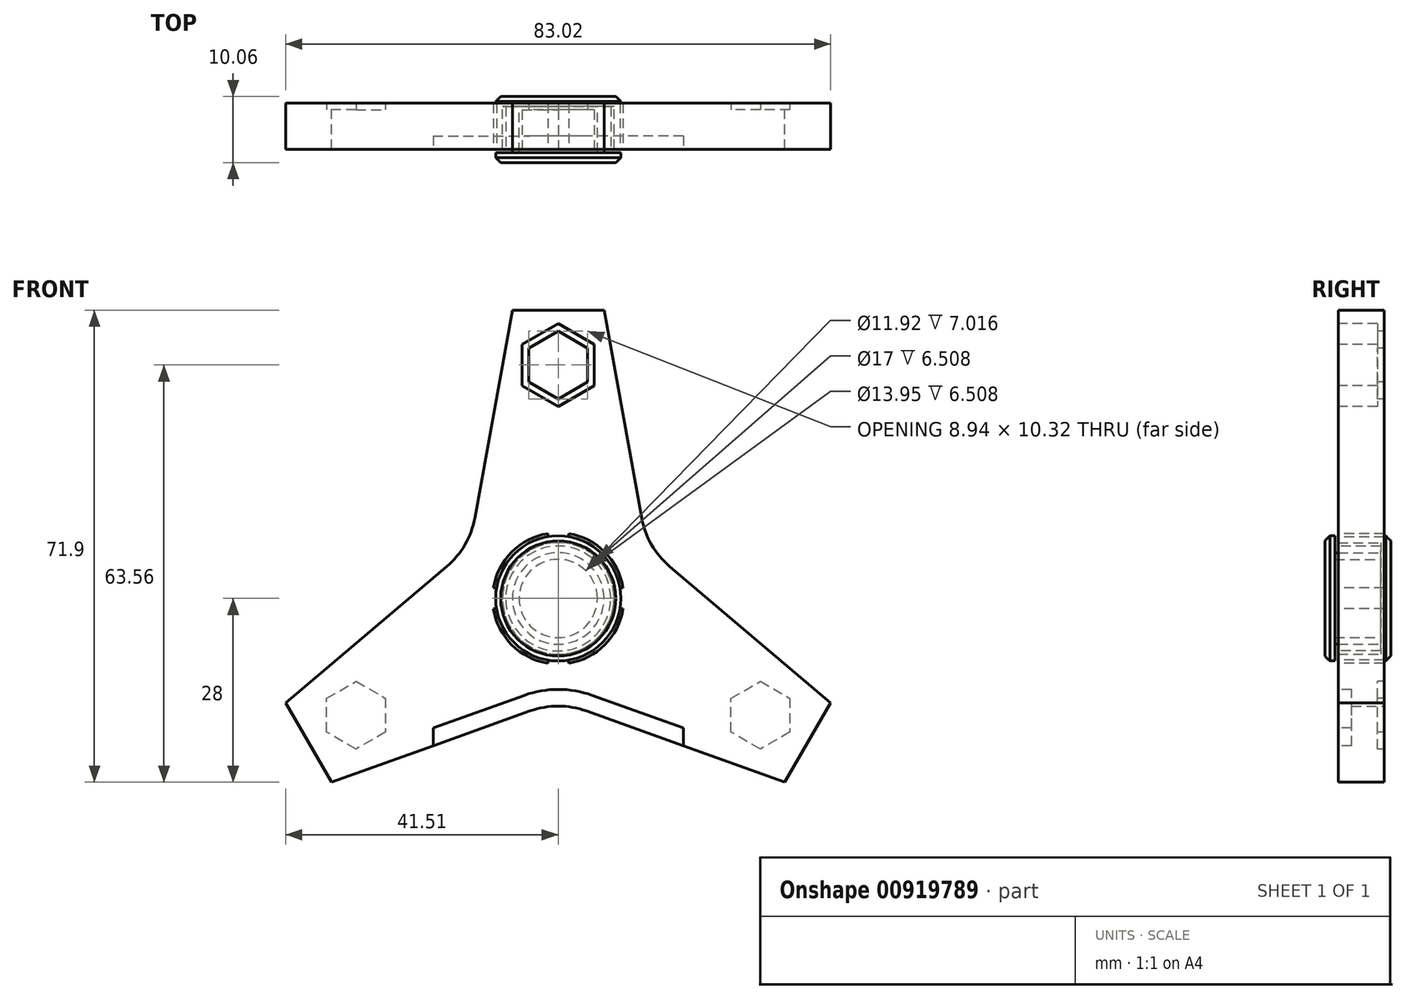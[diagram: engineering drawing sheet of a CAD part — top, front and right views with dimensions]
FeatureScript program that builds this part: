
annotation { "Feature Type Name" : "Feature", "Feature Type Description" : "" }
export const myFeature = defineFeature(function(context is Context, id is Id, definition is map)
    precondition{}
    {
        {
            var Q0;
            Q0=qCreatedBy(makeId("Front.planeOp"),FACE);
            var sketch = newSketch(context, id + "F0", { "sketchPlane" : qUnion([Q0])});
            skCircle(sketch, "E0", {"center": v(0, 0) * mm, "radius": 8.5 * mm});
            skCircle(sketch, "E1.cCircle", {"center": v(0, 0) * mm, "radius": 44.45 * mm, "construction": true});
            skPoint(sketch, "E1.0.midPoint", {"position": v(-38.62, -22) * mm});
            skLineSegment(sketch, "E2", {"start": v(-6.99, 43.9) * mm, "end": v(6.99, 43.9) * mm});
            skLineSegment(sketch, "E3", {"start": v(6.98, 43.9) * mm, "end": v(12.7, 12.29) * mm});
            skLineSegment(sketch, "E4", {"start": v(-6.98, 43.9) * mm, "end": v(-12.7, 12.29) * mm});
            skLineSegment(sketch, "E5.1.0", {"start": v(41.5, -15.9) * mm, "end": v(17, 4.85) * mm});
            skLineSegment(sketch, "E5.1.1", {"start": v(34.52, -28) * mm, "end": v(4.3, -17.14) * mm});
            skLineSegment(sketch, "E5.1.2", {"start": v(41.5, -15.9) * mm, "end": v(34.52, -28) * mm});
            skLineSegment(sketch, "E5.2.0", {"start": v(-34.52, -28) * mm, "end": v(-4.3, -17.14) * mm});
            skLineSegment(sketch, "E5.2.1", {"start": v(-41.5, -15.9) * mm, "end": v(-17, 4.85) * mm});
            skLineSegment(sketch, "E5.2.2", {"start": v(-34.52, -28) * mm, "end": v(-41.5, -15.9) * mm});
            skLineSegment(sketch, "E5.anchor1", {"start": v(0, 0) * mm, "end": v(-14.92, 0) * mm, "construction": true});
            skLineSegment(sketch, "E5.anchor2", {"start": v(0, 0) * mm, "end": v(7.46, -12.92) * mm, "construction": true});
            skPoint(sketch, "E6.orphan", {"position": v(-7.46, 12.92) * mm});
            skPoint(sketch, "E7.orphan", {"position": v(7.46, 12.92) * mm});
            skPoint(sketch, "E8.orphan", {"position": v(-7.46, -12.92) * mm});
            skPoint(sketch, "E9.orphan", {"position": v(14.92, 0) * mm});
            skPoint(sketch, "E10.visualSharp", {"position": v(-13.51, 7.8) * mm});
            skArc(sketch, "E10.filletArc", {"start": v(-17, 4.85) * mm, "mid": v(-14.2, 8.2) * mm, "end": v(-12.7, 12.29) * mm});
            skPoint(sketch, "E11.visualSharp", {"position": v(13.51, 7.8) * mm});
            skArc(sketch, "E11.filletArc", {"start": v(12.7, 12.29) * mm, "mid": v(14.2, 8.2) * mm, "end": v(17, 4.85) * mm});
            skPoint(sketch, "E12.visualSharp", {"position": v(0, -15.6) * mm});
            skArc(sketch, "E12.filletArc", {"start": v(4.3, -17.14) * mm, "mid": v(0, -16.4) * mm, "end": v(-4.3, -17.14) * mm});
            skSolve(sketch);
        }
        {
            var Q0;
            Q0=makeQuery(id+"F0.imprint","IMPRINT",FACE,{"disambiguationData":[TD([[makeQuery(id+"F0.imprint","IMPRINT",EDGE,{"derivedFrom":sQuery(id+"F0.wireOp",EDGE,"E0")}),-1.0]])]});
            extrude(context, id + "F1", {"entities" : qUnion([Q0]), "depth" : 6 * mm, "offsetDistance" : 25.4 * mm});
        }
        {
            var Q0;
            Q0=makeQuery(id+"F1.opExtrude","CAP_FACE",FACE,{"disambiguationData":[OSD([sQuery(id+"F0.wireOp",EDGE,"E0"),sQuery(id+"F0.wireOp",EDGE,"E2"),sQuery(id+"F0.wireOp",EDGE,"E3"),sQuery(id+"F0.wireOp",EDGE,"E4"),sQuery(id+"F0.wireOp",EDGE,"E5.1.0"),sQuery(id+"F0.wireOp",EDGE,"E5.1.1"),sQuery(id+"F0.wireOp",EDGE,"E5.1.2"),sQuery(id+"F0.wireOp",EDGE,"E5.2.0"),sQuery(id+"F0.wireOp",EDGE,"E5.2.1"),sQuery(id+"F0.wireOp",EDGE,"E5.2.2"),sQuery(id+"F0.wireOp",EDGE,"E10.filletArc"),sQuery(id+"F0.wireOp",EDGE,"E11.filletArc"),sQuery(id+"F0.wireOp",EDGE,"E12.filletArc")])],"isStart":false});
            var sketch = newSketch(context, id + "F2", { "sketchPlane" : qUnion([Q0])});
            skCircle(sketch, "E13.0", {"center": v(0, 0) * mm, "radius": 8 * mm});
            skCircle(sketch, "E14.0", {"center": v(0, 0) * mm, "radius": 6.98 * mm});
            skSolve(sketch);
        }
        {
            var Q0;
            Q0=makeQuery(id+"F2.imprint","IMPRINT",FACE,{"disambiguationData":[TD([[makeQuery(id+"F2.imprint","IMPRINT",EDGE,{"derivedFrom":sQuery(id+"F2.wireOp",EDGE,"E13.0")}),1.0]])]});
            var Q1;
            Q1=makeQuery(id+"F1.opExtrude","CAP_FACE",FACE,{"disambiguationData":[OSD([sQuery(id+"F0.wireOp",EDGE,"E0"),sQuery(id+"F0.wireOp",EDGE,"E2"),sQuery(id+"F0.wireOp",EDGE,"E3"),sQuery(id+"F0.wireOp",EDGE,"E4"),sQuery(id+"F0.wireOp",EDGE,"E5.1.0"),sQuery(id+"F0.wireOp",EDGE,"E5.1.1"),sQuery(id+"F0.wireOp",EDGE,"E5.1.2"),sQuery(id+"F0.wireOp",EDGE,"E5.2.0"),sQuery(id+"F0.wireOp",EDGE,"E5.2.1"),sQuery(id+"F0.wireOp",EDGE,"E5.2.2"),sQuery(id+"F0.wireOp",EDGE,"E10.filletArc"),sQuery(id+"F0.wireOp",EDGE,"E11.filletArc"),sQuery(id+"F0.wireOp",EDGE,"E12.filletArc")])],"isStart":true});
            extrude(context, id + "F3", {"entities" : qUnion([Q0]), "endBound" : BoundingType.UP_TO_SURFACE, "oppositeDirection" : true, "depth" : 25.4 * mm, "endBoundEntityFace" : qUnion([Q1]), "hasOffset" : true, "offsetDistance" : 0.5 * mm, "offsetOppositeDirection" : true});
        }
        {
            var Q0;
            Q0=makeQuery(id+"F3.opExtrude","CAP_FACE",FACE,{"disambiguationData":[OSD([sQuery(id+"F2.wireOp",EDGE,"E13.0"),sQuery(id+"F2.wireOp",EDGE,"E14.0")])],"isStart":false});
            var sketch = newSketch(context, id + "F4", { "sketchPlane" : qUnion([Q0])});
            skCircle(sketch, "E15", {"center": v(0, 0) * mm, "radius": 9.53 * mm});
            skSolve(sketch);
        }
        {
            var Q0;
            Q0=makeQuery(id+"F4.imprint","IMPRINT",FACE,{"disambiguationData":[TD([[makeQuery(id+"F4.imprint","IMPRINT",EDGE,{"derivedFrom":sQuery(id+"F4.wireOp",EDGE,"E15")}),1.0]])]});
            var Q1;
            Q1=makeQuery(id+"F4.imprint","IMPRINT",FACE,{"disambiguationData":[TD([[makeQuery(id+"F4.imprint","IMPRINT",EDGE,{"derivedFrom":makeQuery(id+"F3.opExtrude","CAP_EDGE",EDGE,{"disambiguationData":[OSD([sQuery(id+"F2.wireOp",EDGE,"E14.0")])],"isStart":false})}),1.0]])]});
            var Q2;
            Q2=makeQuery(id+"F4.imprint","IMPRINT",FACE,{"disambiguationData":[TD([[makeQuery(id+"F4.imprint","IMPRINT",EDGE,{"derivedFrom":makeQuery(id+"F3.opExtrude","CAP_EDGE",EDGE,{"disambiguationData":[OSD([sQuery(id+"F2.wireOp",EDGE,"E13.0")])],"isStart":false})}),1.0]])]});
            var Q3;
            Q3=sQuery(id+"F4.wireOp",EDGE,"E15");
            extrude(context, id + "F5", {"entities" : qUnion([Q0, Q1, Q2]), "operationType" : NewBodyOperationType.ADD, "surfaceOperationType" : NewSurfaceOperationType.ADD, "surfaceEntities" : qUnion([Q3]), "depth" : 1.52 * mm, "offsetDistance" : 25.4 * mm});
        }
        {
            var Q0;
            Q0=makeQuery(id+"F5.boolean.opBoolean","SPLIT",FACE,{"disambiguationData":[TD([makeQuery(id+"F3.opExtrude","SWEPT_FACE",FACE,{"disambiguationData":[OSD([sQuery(id+"F2.wireOp",EDGE,"E14.0")])]})])],"derivedFrom":makeQuery(id+"F5.opExtrude","CAP_FACE",FACE,{"disambiguationData":[OSD([sQuery(id+"F4.wireOp",EDGE,"E15")])],"isStart":true})});
            var sketch = newSketch(context, id + "F6", { "sketchPlane" : qUnion([Q0])});
            skCircle(sketch, "E16.0", {"center": v(0, 0) * mm, "radius": 6.98 * mm});
            skCircle(sketch, "E17.0", {"center": v(0, 0) * mm, "radius": 5.96 * mm});
            skSolve(sketch);
        }
        {
            var Q0;
            Q0=makeQuery(id+"F6.imprint","IMPRINT",FACE,{"disambiguationData":[TD([[makeQuery(id+"F6.imprint","IMPRINT",EDGE,{"derivedFrom":sQuery(id+"F6.wireOp",EDGE,"E16.0")}),-1.0]])]});
            var Q1;
            Q1=sQuery(id+"F6.wireOp",EDGE,"E16.0");
            var Q2;
            Q2=makeQuery(id+"F1.opExtrude","CAP_FACE",FACE,{"disambiguationData":[OSD([sQuery(id+"F0.wireOp",EDGE,"E0"),sQuery(id+"F0.wireOp",EDGE,"E2"),sQuery(id+"F0.wireOp",EDGE,"E3"),sQuery(id+"F0.wireOp",EDGE,"E4"),sQuery(id+"F0.wireOp",EDGE,"E5.1.0"),sQuery(id+"F0.wireOp",EDGE,"E5.1.1"),sQuery(id+"F0.wireOp",EDGE,"E5.1.2"),sQuery(id+"F0.wireOp",EDGE,"E5.2.0"),sQuery(id+"F0.wireOp",EDGE,"E5.2.1"),sQuery(id+"F0.wireOp",EDGE,"E5.2.2"),sQuery(id+"F0.wireOp",EDGE,"E10.filletArc"),sQuery(id+"F0.wireOp",EDGE,"E11.filletArc"),sQuery(id+"F0.wireOp",EDGE,"E12.filletArc")])],"isStart":false});
            extrude(context, id + "F7", {"entities" : qUnion([Q0]), "surfaceEntities" : qUnion([Q1]), "endBound" : BoundingType.UP_TO_SURFACE, "depth" : 25.4 * mm, "endBoundEntityFace" : qUnion([Q2]), "hasOffset" : true, "offsetDistance" : 0.5 * mm, "offsetOppositeDirection" : true});
        }
        {
            var Q0;
            Q0=makeQuery(id+"F7.opExtrude","CAP_FACE",FACE,{"disambiguationData":[OSD([sQuery(id+"F6.wireOp",EDGE,"E16.0"),sQuery(id+"F6.wireOp",EDGE,"E17.0")])],"isStart":false});
            var sketch = newSketch(context, id + "F8", { "sketchPlane" : qUnion([Q0])});
            skCircle(sketch, "E18.0", {"center": v(0, 0) * mm, "radius": 9.53 * mm});
            skSolve(sketch);
        }
        {
            var Q0;
            Q0=makeQuery(id+"F8.imprint","IMPRINT",FACE,{"disambiguationData":[TD([[makeQuery(id+"F8.imprint","IMPRINT",EDGE,{"derivedFrom":sQuery(id+"F8.wireOp",EDGE,"E18.0")}),1.0]])]});
            var Q1;
            Q1=makeQuery(id+"F8.imprint","IMPRINT",FACE,{"disambiguationData":[TD([[makeQuery(id+"F8.imprint","IMPRINT",EDGE,{"derivedFrom":makeQuery(id+"F7.opExtrude","CAP_EDGE",EDGE,{"disambiguationData":[OSD([sQuery(id+"F6.wireOp",EDGE,"E16.0")])],"isStart":false})}),-1.0]])]});
            var Q2;
            Q2=makeQuery(id+"F8.imprint","IMPRINT",FACE,{"disambiguationData":[TD([[makeQuery(id+"F8.imprint","IMPRINT",EDGE,{"derivedFrom":makeQuery(id+"F7.opExtrude","CAP_EDGE",EDGE,{"disambiguationData":[OSD([sQuery(id+"F6.wireOp",EDGE,"E17.0")])],"isStart":false})}),1.0]])]});
            extrude(context, id + "F9", {"entities" : qUnion([Q0, Q1, Q2]), "operationType" : NewBodyOperationType.ADD, "depth" : 1.52 * mm, "offsetDistance" : 25.4 * mm});
        }
        {
            var Q0;
            Q0=makeQuery(id+"F5.opExtrude","CAP_EDGE",EDGE,{"disambiguationData":[OSD([sQuery(id+"F4.wireOp",EDGE,"E15")])],"isStart":false});
            var Q1;
            Q1=makeQuery(id+"F9.opExtrude","CAP_EDGE",EDGE,{"disambiguationData":[OSD([sQuery(id+"F8.wireOp",EDGE,"E18.0")])],"isStart":false});
            chamfer(context, id + "F10", {"entities" : qUnion([Q0, Q1]), "width" : 0.76 * mm, "tangentPropagation" : true});
        }
        {
            var Q0;
            Q0=makeQuery(id+"F1.opExtrude","CAP_FACE",FACE,{"disambiguationData":[OSD([sQuery(id+"F0.wireOp",EDGE,"E0"),sQuery(id+"F0.wireOp",EDGE,"E2"),sQuery(id+"F0.wireOp",EDGE,"E3"),sQuery(id+"F0.wireOp",EDGE,"E4"),sQuery(id+"F0.wireOp",EDGE,"E5.1.0"),sQuery(id+"F0.wireOp",EDGE,"E5.1.1"),sQuery(id+"F0.wireOp",EDGE,"E5.1.2"),sQuery(id+"F0.wireOp",EDGE,"E5.2.0"),sQuery(id+"F0.wireOp",EDGE,"E5.2.1"),sQuery(id+"F0.wireOp",EDGE,"E5.2.2"),sQuery(id+"F0.wireOp",EDGE,"E10.filletArc"),sQuery(id+"F0.wireOp",EDGE,"E11.filletArc"),sQuery(id+"F0.wireOp",EDGE,"E12.filletArc")])],"isStart":false});
            var sketch = newSketch(context, id + "F11", { "sketchPlane" : qUnion([Q0])});
            skCircle(sketch, "E19.cCircle", {"center": v(0, 35.56) * mm, "radius": 5.49 * mm, "construction": true});
            skLineSegment(sketch, "E19.0", {"start": v(5.49, 32.4) * mm, "end": v(0, 29.22) * mm});
            skLineSegment(sketch, "E19.1", {"start": v(0, 29.22) * mm, "end": v(-5.49, 32.4) * mm});
            skLineSegment(sketch, "E19.2", {"start": v(-5.49, 32.4) * mm, "end": v(-5.49, 38.73) * mm});
            skLineSegment(sketch, "E19.3", {"start": v(-5.49, 38.73) * mm, "end": v(0, 41.9) * mm});
            skLineSegment(sketch, "E19.4", {"start": v(0, 41.9) * mm, "end": v(5.49, 38.73) * mm});
            skLineSegment(sketch, "E19.5", {"start": v(5.49, 38.73) * mm, "end": v(5.49, 32.4) * mm});
            skPoint(sketch, "E19.0.midPoint", {"position": v(2.74, 30.8) * mm});
            skSolve(sketch);
        }
        {
            var Q0;
            Q0=makeQuery(id+"F11.imprint","IMPRINT",FACE,{"disambiguationData":[TD([[makeQuery(id+"F11.imprint","IMPRINT",EDGE,{"derivedFrom":sQuery(id+"F11.wireOp",EDGE,"E19.0")}),-1.0]])]});
            extrude(context, id + "F12", {"entities" : qUnion([Q0]), "operationType" : NewBodyOperationType.REMOVE, "endBound" : BoundingType.THROUGH_ALL, "oppositeDirection" : true, "depth" : 25.4 * mm, "offsetDistance" : 25.4 * mm});
        }
        {
            var Q0;
            Q0=makeQuery(id+"F1.opExtrude","CAP_FACE",FACE,{"disambiguationData":[OSD([sQuery(id+"F0.wireOp",EDGE,"E0"),sQuery(id+"F0.wireOp",EDGE,"E2"),sQuery(id+"F0.wireOp",EDGE,"E3"),sQuery(id+"F0.wireOp",EDGE,"E4"),sQuery(id+"F0.wireOp",EDGE,"E5.1.0"),sQuery(id+"F0.wireOp",EDGE,"E5.1.1"),sQuery(id+"F0.wireOp",EDGE,"E5.1.2"),sQuery(id+"F0.wireOp",EDGE,"E5.2.0"),sQuery(id+"F0.wireOp",EDGE,"E5.2.1"),sQuery(id+"F0.wireOp",EDGE,"E5.2.2"),sQuery(id+"F0.wireOp",EDGE,"E10.filletArc"),sQuery(id+"F0.wireOp",EDGE,"E11.filletArc"),sQuery(id+"F0.wireOp",EDGE,"E12.filletArc")])],"isStart":false});
            var sketch = newSketch(context, id + "F13", { "sketchPlane" : qUnion([Q0])});
            skArc(sketch, "E20", {"start": v(-1.59, 9.88) * mm, "mid": v(-7.07, 7.07) * mm, "end": v(-9.88, 1.59) * mm});
            skArc(sketch, "E21.trimOffspring", {"start": v(1.59, -9.88) * mm, "mid": v(7.07, -7.07) * mm, "end": v(9.88, -1.59) * mm});
            skPoint(sketch, "E22.orphan", {"position": v(0.39, -10) * mm});
            skArc(sketch, "E23.trimOffspring", {"start": v(9.88, 1.59) * mm, "mid": v(7.07, 7.07) * mm, "end": v(1.59, 9.88) * mm});
            skArc(sketch, "E24.trimOffspring", {"start": v(-9.88, -1.59) * mm, "mid": v(-7.07, -7.07) * mm, "end": v(-1.59, -9.88) * mm});
            skLineSegment(sketch, "E25", {"start": v(-1.59, 9.88) * mm, "end": v(-1.59, 9.4) * mm});
            skLineSegment(sketch, "E26", {"start": v(1.59, 9.4) * mm, "end": v(1.59, 9.88) * mm});
            skLineSegment(sketch, "E27", {"start": v(-9.88, 1.59) * mm, "end": v(-9.38, 1.59) * mm});
            skLineSegment(sketch, "E28", {"start": v(-9.88, -1.59) * mm, "end": v(-9.4, -1.59) * mm});
            skLineSegment(sketch, "E29", {"start": v(9.88, 1.59) * mm, "end": v(9.38, 1.59) * mm});
            skLineSegment(sketch, "E30", {"start": v(9.88, -1.59) * mm, "end": v(9.39, -1.59) * mm});
            skLineSegment(sketch, "E31", {"start": v(-1.59, -9.88) * mm, "end": v(-1.59, -9.4) * mm});
            skLineSegment(sketch, "E32", {"start": v(1.59, -9.88) * mm, "end": v(1.59, -9.4) * mm});
            skArc(sketch, "E33", {"start": v(1.59, -9.4) * mm, "mid": v(6.74, -6.74) * mm, "end": v(9.4, -1.59) * mm});
            skArc(sketch, "E34.trimOffspring", {"start": v(-9.4, -1.59) * mm, "mid": v(-6.74, -6.74) * mm, "end": v(-1.59, -9.4) * mm});
            skArc(sketch, "E35.trimOffspring", {"start": v(9.4, 1.59) * mm, "mid": v(6.74, 6.74) * mm, "end": v(1.59, 9.4) * mm});
            skArc(sketch, "E36.trimOffspring", {"start": v(-1.59, 9.4) * mm, "mid": v(-6.74, 6.74) * mm, "end": v(-9.4, 1.59) * mm});
            skPoint(sketch, "E37.orphan", {"position": v(1.59, 9.15) * mm});
            skSolve(sketch);
        }
        {
            var Q0;
            {var subQ0=sQuery(id+"F13.wireOp",EDGE,"E20");Q0=makeQuery(id+"F13.imprint","IMPRINT",FACE,{"disambiguationData":[TD([[makeQuery(id+"F13.imprint","IMPRINT",EDGE,{"derivedFrom":subQ0}),1.0]])]});}
            var Q1;
            {var subQ0=sQuery(id+"F13.wireOp",EDGE,"E23.trimOffspring");Q1=makeQuery(id+"F13.imprint","IMPRINT",FACE,{"disambiguationData":[TD([[makeQuery(id+"F13.imprint","IMPRINT",EDGE,{"derivedFrom":subQ0}),1.0]])]});}
            var Q2;
            {var subQ0=sQuery(id+"F13.wireOp",EDGE,"E24.trimOffspring");Q2=makeQuery(id+"F13.imprint","IMPRINT",FACE,{"disambiguationData":[TD([[makeQuery(id+"F13.imprint","IMPRINT",EDGE,{"derivedFrom":subQ0}),1.0]])]});}
            var Q3;
            {var subQ0=sQuery(id+"F13.wireOp",EDGE,"E21.trimOffspring");Q3=makeQuery(id+"F13.imprint","IMPRINT",FACE,{"disambiguationData":[TD([[makeQuery(id+"F13.imprint","IMPRINT",EDGE,{"derivedFrom":subQ0}),1.0]])]});}
            extrude(context, id + "F14", {"entities" : qUnion([Q0, Q1, Q2, Q3]), "operationType" : NewBodyOperationType.REMOVE, "endBound" : BoundingType.THROUGH_ALL, "oppositeDirection" : true, "depth" : 5.08 * mm, "offsetDistance" : 25.4 * mm});
        }
        {
            var Q0;
            Q0=makeQuery(id+"F1.opExtrude","CAP_FACE",FACE,{"disambiguationData":[OSD([sQuery(id+"F0.wireOp",EDGE,"E0"),sQuery(id+"F0.wireOp",EDGE,"E2"),sQuery(id+"F0.wireOp",EDGE,"E3"),sQuery(id+"F0.wireOp",EDGE,"E4"),sQuery(id+"F0.wireOp",EDGE,"E5.1.0"),sQuery(id+"F0.wireOp",EDGE,"E5.1.1"),sQuery(id+"F0.wireOp",EDGE,"E5.1.2"),sQuery(id+"F0.wireOp",EDGE,"E5.2.0"),sQuery(id+"F0.wireOp",EDGE,"E5.2.1"),sQuery(id+"F0.wireOp",EDGE,"E5.2.2"),sQuery(id+"F0.wireOp",EDGE,"E10.filletArc"),sQuery(id+"F0.wireOp",EDGE,"E11.filletArc"),sQuery(id+"F0.wireOp",EDGE,"E12.filletArc")])],"isStart":false});
            var sketch = newSketch(context, id + "F15", { "sketchPlane" : qUnion([Q0])});
            skPoint(sketch, "E38.orphan", {"position": v(41.5, -15.9) * mm});
            skPoint(sketch, "E39.orphan", {"position": v(6.98, 43.9) * mm});
            skPoint(sketch, "E40.orphan", {"position": v(-41.5, -15.9) * mm});
            skPoint(sketch, "E41.orphan", {"position": v(-6.98, 43.9) * mm});
            skLineSegment(sketch, "E42.0", {"start": v(-19.05, -19.74) * mm, "end": v(-5.15, -14.75) * mm});
            skArc(sketch, "E42.1", {"start": v(5.15, -14.75) * mm, "mid": v(0, -13.86) * mm, "end": v(-5.15, -14.75) * mm});
            skLineSegment(sketch, "E42.2", {"start": v(19.05, -19.74) * mm, "end": v(5.15, -14.75) * mm});
            skLineSegment(sketch, "E43", {"start": v(-19.05, -22.44) * mm, "end": v(-19.05, -19.74) * mm});
            skLineSegment(sketch, "E44", {"start": v(19.05, -19.74) * mm, "end": v(19.05, -22.44) * mm});
            skLineSegment(sketch, "E45.0", {"start": v(-19.05, -22.44) * mm, "end": v(-4.3, -17.14) * mm});
            skLineSegment(sketch, "E45.1", {"start": v(19.05, -22.44) * mm, "end": v(4.3, -17.14) * mm});
            skArc(sketch, "E45.2", {"start": v(4.3, -17.14) * mm, "mid": v(0, -16.4) * mm, "end": v(-4.3, -17.14) * mm});
            skPoint(sketch, "E46.orphan", {"position": v(34.52, -28) * mm});
            skPoint(sketch, "E47.orphan", {"position": v(-34.52, -28) * mm});
            skSolve(sketch);
        }
        {
            var Q0;
            Q0=makeQuery(id+"F15.imprint","IMPRINT",FACE,{"disambiguationData":[TD([[makeQuery(id+"F15.imprint","IMPRINT",EDGE,{"derivedFrom":sQuery(id+"F15.wireOp",EDGE,"E42.0")}),-1.0]])]});
            extrude(context, id + "F16", {"entities" : qUnion([Q0]), "operationType" : NewBodyOperationType.REMOVE, "oppositeDirection" : true, "depth" : 2.03 * mm, "offsetDistance" : 25.4 * mm});
        }
        {
            var Q0;
            Q0=makeQuery(id+"F1.opExtrude","CAP_FACE",FACE,{"disambiguationData":[OSD([sQuery(id+"F0.wireOp",EDGE,"E0"),sQuery(id+"F0.wireOp",EDGE,"E2"),sQuery(id+"F0.wireOp",EDGE,"E3"),sQuery(id+"F0.wireOp",EDGE,"E4"),sQuery(id+"F0.wireOp",EDGE,"E5.1.0"),sQuery(id+"F0.wireOp",EDGE,"E5.1.1"),sQuery(id+"F0.wireOp",EDGE,"E5.1.2"),sQuery(id+"F0.wireOp",EDGE,"E5.2.0"),sQuery(id+"F0.wireOp",EDGE,"E5.2.1"),sQuery(id+"F0.wireOp",EDGE,"E5.2.2"),sQuery(id+"F0.wireOp",EDGE,"E10.filletArc"),sQuery(id+"F0.wireOp",EDGE,"E11.filletArc"),sQuery(id+"F0.wireOp",EDGE,"E12.filletArc")])],"isStart":false});
            var Q1;
            Q1=makeQuery(id+"F1.opExtrude","CAP_FACE",FACE,{"disambiguationData":[OSD([sQuery(id+"F0.wireOp",EDGE,"E0"),sQuery(id+"F0.wireOp",EDGE,"E2"),sQuery(id+"F0.wireOp",EDGE,"E3"),sQuery(id+"F0.wireOp",EDGE,"E4"),sQuery(id+"F0.wireOp",EDGE,"E5.1.0"),sQuery(id+"F0.wireOp",EDGE,"E5.1.1"),sQuery(id+"F0.wireOp",EDGE,"E5.1.2"),sQuery(id+"F0.wireOp",EDGE,"E5.2.0"),sQuery(id+"F0.wireOp",EDGE,"E5.2.1"),sQuery(id+"F0.wireOp",EDGE,"E5.2.2"),sQuery(id+"F0.wireOp",EDGE,"E10.filletArc"),sQuery(id+"F0.wireOp",EDGE,"E11.filletArc"),sQuery(id+"F0.wireOp",EDGE,"E12.filletArc")])],"isStart":true});
            cPlane(context, id + "F17", {"entities" : qUnion([Q0, Q1]), "cplaneType" : CPlaneType.MID_PLANE, "offset" : 25.4 * mm, "width" : 152.4 * mm, "height" : 152.4 * mm});
        }
        {
            var Q0;
            Q0=makeQuery(id+"F1.opExtrude","CAP_FACE",FACE,{"disambiguationData":[OSD([sQuery(id+"F0.wireOp",EDGE,"E0"),sQuery(id+"F0.wireOp",EDGE,"E2"),sQuery(id+"F0.wireOp",EDGE,"E3"),sQuery(id+"F0.wireOp",EDGE,"E4"),sQuery(id+"F0.wireOp",EDGE,"E5.1.0"),sQuery(id+"F0.wireOp",EDGE,"E5.1.1"),sQuery(id+"F0.wireOp",EDGE,"E5.1.2"),sQuery(id+"F0.wireOp",EDGE,"E5.2.0"),sQuery(id+"F0.wireOp",EDGE,"E5.2.1"),sQuery(id+"F0.wireOp",EDGE,"E5.2.2"),sQuery(id+"F0.wireOp",EDGE,"E10.filletArc"),sQuery(id+"F0.wireOp",EDGE,"E11.filletArc"),sQuery(id+"F0.wireOp",EDGE,"E12.filletArc")])],"isStart":true});
            var sketch = newSketch(context, id + "F18", { "sketchPlane" : qUnion([Q0])});
            skLineSegment(sketch, "E48.0", {"start": v(4.47, 32.98) * mm, "end": v(4.47, 38.14) * mm});
            skLineSegment(sketch, "E48.1", {"start": v(0, 40.72) * mm, "end": v(-4.47, 38.14) * mm});
            skLineSegment(sketch, "E48.2", {"start": v(-4.47, 38.14) * mm, "end": v(-4.47, 32.98) * mm});
            skLineSegment(sketch, "E48.3", {"start": v(4.47, 38.14) * mm, "end": v(0, 40.72) * mm});
            skLineSegment(sketch, "E48.4", {"start": v(-4.47, 32.98) * mm, "end": v(0, 30.4) * mm});
            skLineSegment(sketch, "E48.5", {"start": v(0, 30.4) * mm, "end": v(4.47, 32.98) * mm});
            skLineSegment(sketch, "E49.1.0", {"start": v(-30.8, -12.62) * mm, "end": v(-35.27, -15.2) * mm});
            skLineSegment(sketch, "E49.1.1", {"start": v(-26.33, -15.2) * mm, "end": v(-30.8, -12.62) * mm});
            skLineSegment(sketch, "E49.1.2", {"start": v(-26.33, -20.36) * mm, "end": v(-26.33, -15.2) * mm});
            skLineSegment(sketch, "E49.1.3", {"start": v(-30.8, -22.94) * mm, "end": v(-26.33, -20.36) * mm});
            skLineSegment(sketch, "E49.1.4", {"start": v(-35.27, -20.36) * mm, "end": v(-30.8, -22.94) * mm});
            skLineSegment(sketch, "E49.1.5", {"start": v(-35.27, -15.2) * mm, "end": v(-35.27, -20.36) * mm});
            skLineSegment(sketch, "E49.2.0", {"start": v(26.33, -20.36) * mm, "end": v(30.8, -22.94) * mm});
            skLineSegment(sketch, "E49.2.1", {"start": v(26.33, -15.2) * mm, "end": v(26.33, -20.36) * mm});
            skLineSegment(sketch, "E49.2.2", {"start": v(30.8, -12.62) * mm, "end": v(26.33, -15.2) * mm});
            skLineSegment(sketch, "E49.2.3", {"start": v(35.27, -15.2) * mm, "end": v(30.8, -12.62) * mm});
            skLineSegment(sketch, "E49.2.4", {"start": v(35.27, -20.36) * mm, "end": v(35.27, -15.2) * mm});
            skLineSegment(sketch, "E49.2.5", {"start": v(30.8, -22.94) * mm, "end": v(35.27, -20.36) * mm});
            skPoint(sketch, "E49.center", {"position": v(0, 0) * mm});
            skSolve(sketch);
        }
        {
            var Q0;
            {var subQ15=sQuery(id+"F0.wireOp",EDGE,"E0");Q0=makeQuery(id+"F18.imprint","IMPRINT",FACE,{"disambiguationData":[TD([[makeQuery(id+"F18.imprint","IMPRINT",EDGE,{"derivedFrom":makeQuery(id+"F1.opExtrude","CAP_EDGE",EDGE,{"disambiguationData":[OSD([subQ15])],"isStart":true})}),1.0]])]});}
            var Q1;
            Q1=makeQuery(id+"F18.imprint","IMPRINT",FACE,{"disambiguationData":[TD([[makeQuery(id+"F18.imprint","IMPRINT",EDGE,{"derivedFrom":sQuery(id+"F18.wireOp",EDGE,"E48.0")}),-1.0]])]});
            var Q2;
            Q2=makeQuery(id+"F18.imprint","IMPRINT",FACE,{"disambiguationData":[TD([[makeQuery(id+"F18.imprint","IMPRINT",EDGE,{"derivedFrom":sQuery(id+"F18.wireOp",EDGE,"E49.2.0")}),-1.0]])]});
            var Q3;
            Q3=makeQuery(id+"F18.imprint","IMPRINT",FACE,{"disambiguationData":[TD([[makeQuery(id+"F18.imprint","IMPRINT",EDGE,{"derivedFrom":sQuery(id+"F18.wireOp",EDGE,"E49.1.0")}),-1.0]])]});
            extrude(context, id + "F19", {"entities" : qUnion([Q0, Q1, Q2, Q3]), "operationType" : NewBodyOperationType.ADD, "depth" : 1.02 * mm, "offsetDistance" : 25.4 * mm});
        }
    });
